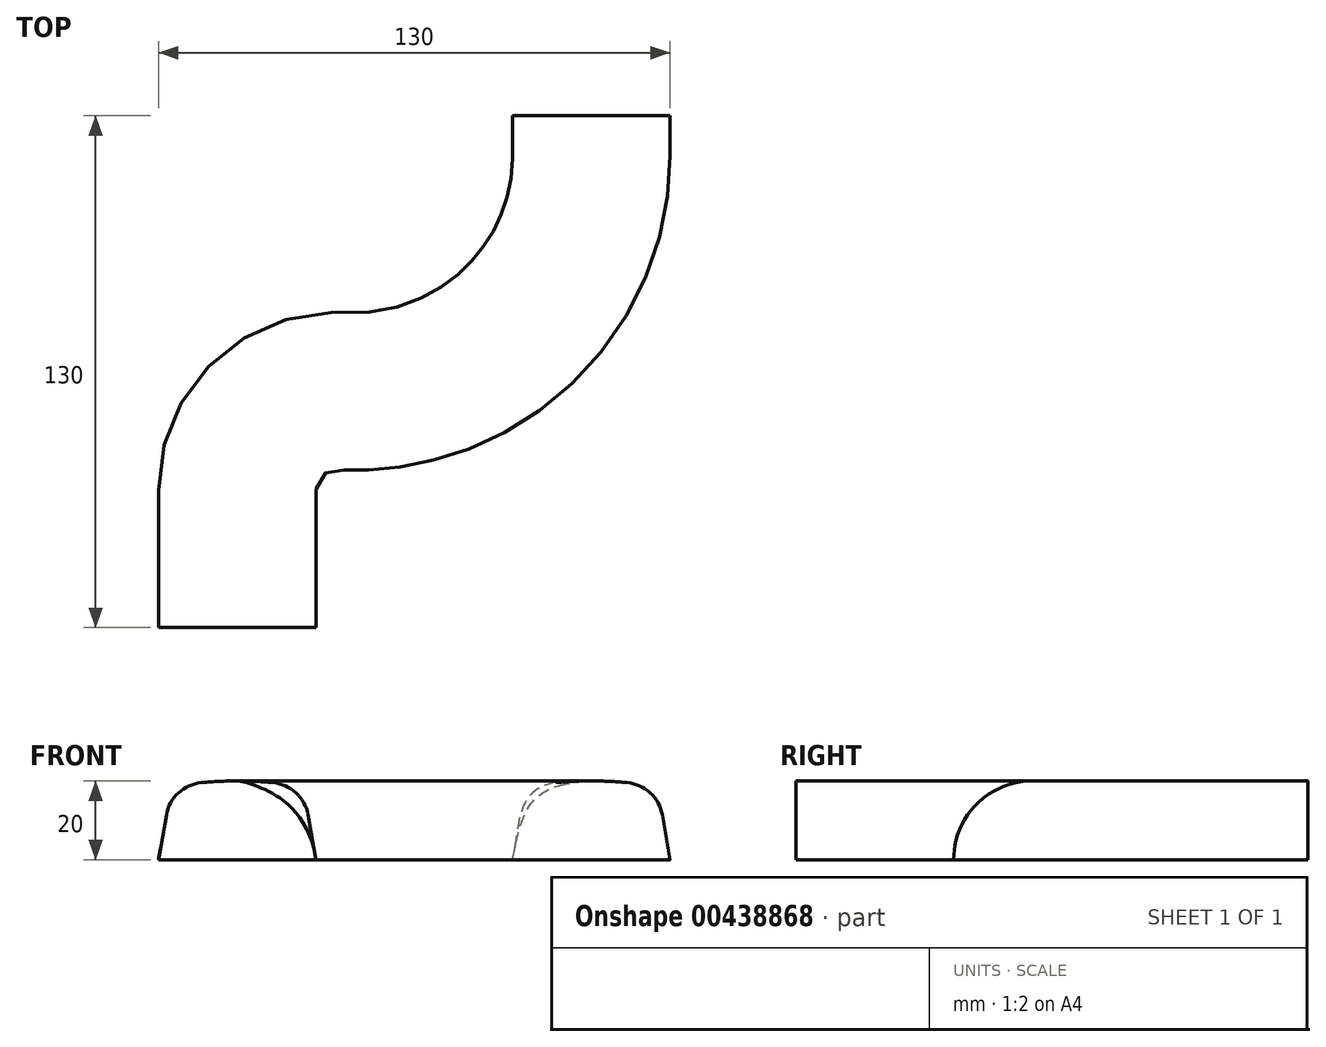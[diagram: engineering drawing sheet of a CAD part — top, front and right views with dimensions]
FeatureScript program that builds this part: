
annotation { "Feature Type Name" : "Feature", "Feature Type Description" : "" }
export const myFeature = defineFeature(function(context is Context, id is Id, definition is map)
    precondition{}
    {
        {
            var Q0;
            Q0=qCreatedBy(makeId("Top.planeOp"),FACE);
            var sketch = newSketch(context, id + "F0", { "sketchPlane" : qUnion([Q0])});
            skLineSegment(sketch, "E0", {"start": v(-30, -60) * mm, "end": v(-30, -25) * mm});
            skLineSegment(sketch, "E1", {"start": v(-5, 0) * mm, "end": v(0, 0) * mm});
            skLineSegment(sketch, "E2", {"start": v(60, 60) * mm, "end": v(60, 70) * mm});
            skArc(sketch, "E3.filletArc", {"start": v(0, 0) * mm, "mid": v(42.43, 17.57) * mm, "end": v(60, 60) * mm});
            skPoint(sketch, "E4.visualSharp", {"position": v(-30, 0) * mm});
            skArc(sketch, "E4.filletArc", {"start": v(-5, 0) * mm, "mid": v(-22.68, -7.32) * mm, "end": v(-30, -25) * mm});
            skSolve(sketch);
        }
        {
            var Q0;
            Q0=sQuery(id+"F0.wireOp",VERTEX,"E0.start");
            var Q1;
            Q1=sQuery(id+"F0.wireOp",EDGE,"E0");
            cPlane(context, id + "F1", {"entities" : qUnion([Q0, Q1]), "cplaneType" : CPlaneType.LINE_POINT, "offset" : 25 * mm, "width" : 150 * mm, "height" : 150 * mm});
        }
        {
            var Q0;
            Q0=sQuery(id+"F0.wireOp",VERTEX,"E2.end");
            var Q1;
            Q1=sQuery(id+"F0.wireOp",EDGE,"E2");
            cPlane(context, id + "F2", {"entities" : qUnion([Q0, Q1]), "cplaneType" : CPlaneType.LINE_POINT, "offset" : 25 * mm, "width" : 150 * mm, "height" : 150 * mm});
        }
        {
            var Q0;
            Q0=qCreatedBy(id+"F1.planeOp",FACE);
            var sketch = newSketch(context, id + "F3", { "sketchPlane" : qUnion([Q0])});
            skLineSegment(sketch, "E5", {"start": v(30, 0) * mm, "end": v(30, -10) * mm, "construction": true});
            skLineSegment(sketch, "E6.bottom", {"start": v(10, -20) * mm, "end": v(50, -20) * mm, "construction": true});
            skLineSegment(sketch, "E6.top", {"start": v(10, 0) * mm, "end": v(50, 0) * mm, "construction": true});
            skLineSegment(sketch, "E6.left", {"start": v(10, -20) * mm, "end": v(10, 0) * mm, "construction": true});
            skLineSegment(sketch, "E6.right", {"start": v(50, -20) * mm, "end": v(50, 0) * mm, "construction": true});
            skPoint(sketch, "E6.middle", {"position": v(30, -10) * mm});
            skLineSegment(sketch, "E7", {"start": v(50, -20) * mm, "end": v(48, -8.63) * mm});
            skLineSegment(sketch, "E8.MirrorCS", {"start": v(10, -20) * mm, "end": v(12, -8.63) * mm});
            skArc(sketch, "E9", {"start": v(39.05, -0.41) * mm, "mid": v(30, 0) * mm, "end": v(20.95, -0.41) * mm});
            skPoint(sketch, "E10.visualSharp", {"position": v(46.72, -1.4) * mm});
            skArc(sketch, "E10.filletArc", {"start": v(48, -8.63) * mm, "mid": v(44.92, -3) * mm, "end": v(39.05, -0.41) * mm});
            skPoint(sketch, "E11.visualSharp", {"position": v(13.28, -1.4) * mm});
            skArc(sketch, "E11.filletArc", {"start": v(20.95, -0.41) * mm, "mid": v(15.08, -3) * mm, "end": v(12, -8.63) * mm});
            skSolve(sketch);
        }
        {
            var Q0;
            Q0=qCreatedBy(makeId("Right.planeOp"),FACE);
            var sketch = newSketch(context, id + "F4", { "sketchPlane" : qUnion([Q0])});
            skLineSegment(sketch, "E12", {"start": v(0, 0) * mm, "end": v(0, -20) * mm, "construction": true});
            skArc(sketch, "E13", {"start": v(20, -20) * mm, "mid": v(0, 0) * mm, "end": v(-20, -20) * mm});
            skSolve(sketch);
        }
        {
            var Q0;
            Q0=qCreatedBy(id+"F2.planeOp",FACE);
            var sketch = newSketch(context, id + "F5", { "sketchPlane" : qUnion([Q0])});
            skLineSegment(sketch, "E14", {"start": v(-60, 0) * mm, "end": v(-60, -10) * mm, "construction": true});
            skLineSegment(sketch, "E15.bottom", {"start": v(-40, -20) * mm, "end": v(-80, -20) * mm, "construction": true});
            skLineSegment(sketch, "E15.top", {"start": v(-40, 0) * mm, "end": v(-80, 0) * mm, "construction": true});
            skLineSegment(sketch, "E15.left", {"start": v(-40, -20) * mm, "end": v(-40, 0) * mm, "construction": true});
            skLineSegment(sketch, "E15.right", {"start": v(-80, -20) * mm, "end": v(-80, 0) * mm, "construction": true});
            skPoint(sketch, "E15.middle", {"position": v(-60, -10) * mm});
            skLineSegment(sketch, "E16", {"start": v(-80, -20) * mm, "end": v(-78, -8.63) * mm});
            skLineSegment(sketch, "E17.MirrorCS", {"start": v(-40, -20) * mm, "end": v(-42, -8.63) * mm});
            skArc(sketch, "E18", {"start": v(-50.95, -0.41) * mm, "mid": v(-60, 0) * mm, "end": v(-69.05, -0.41) * mm});
            skPoint(sketch, "E19.visualSharp", {"position": v(-76.72, -1.4) * mm});
            skArc(sketch, "E19.filletArc", {"start": v(-69.05, -0.41) * mm, "mid": v(-74.92, -3) * mm, "end": v(-78, -8.63) * mm});
            skPoint(sketch, "E20.visualSharp", {"position": v(-43.28, -1.4) * mm});
            skArc(sketch, "E20.filletArc", {"start": v(-42, -8.63) * mm, "mid": v(-45.08, -3) * mm, "end": v(-50.95, -0.41) * mm});
            skSolve(sketch);
        }
        {
            var Q0;
            Q0=qCreatedBy(makeId("Top.planeOp"),FACE);
            cPlane(context, id + "F6", {"entities" : qUnion([Q0]), "cplaneType" : CPlaneType.OFFSET, "offset" : 20 * mm, "oppositeDirection" : true, "width" : 150 * mm, "height" : 150 * mm});
        }
        {
            var Q0;
            Q0=qCreatedBy(id+"F6.planeOp",FACE);
            var sketch = newSketch(context, id + "F7", { "sketchPlane" : qUnion([Q0])});
            skLineSegment(sketch, "E21.0", {"start": v(40, 60) * mm, "end": v(40, 70) * mm});
            skLineSegment(sketch, "E21.1", {"start": v(-50, -60) * mm, "end": v(-50, -25) * mm});
            skArc(sketch, "E21.2", {"start": v(-5, 20) * mm, "mid": v(-36.82, 6.82) * mm, "end": v(-50, -25) * mm});
            skLineSegment(sketch, "E21.3", {"start": v(-5, 20) * mm, "end": v(0, 20) * mm});
            skArc(sketch, "E21.4", {"start": v(0, 20) * mm, "mid": v(28.28, 31.72) * mm, "end": v(40, 60) * mm});
            skSolve(sketch);
        }
        {
            var Q0;
            Q0=qCreatedBy(id+"F6.planeOp",FACE);
            var sketch = newSketch(context, id + "F8", { "sketchPlane" : qUnion([Q0])});
            skLineSegment(sketch, "E22.0", {"start": v(80, 60) * mm, "end": v(80, 70) * mm});
            skLineSegment(sketch, "E22.1", {"start": v(-10, -60) * mm, "end": v(-10, -25) * mm});
            skArc(sketch, "E22.2", {"start": v(-5, -20) * mm, "mid": v(-8.54, -21.46) * mm, "end": v(-10, -25) * mm});
            skLineSegment(sketch, "E22.3", {"start": v(-5, -20) * mm, "end": v(0, -20) * mm});
            skArc(sketch, "E22.4", {"start": v(0, -20) * mm, "mid": v(56.57, 3.43) * mm, "end": v(80, 60) * mm});
            skSolve(sketch);
        }
        {
            var Q0;
            Q0 = qConstructionFilter(qBodyType(qCreatedBy(id + "F3" ,EDGE), BodyType.WIRE), ConstructionObject.NO);
            var Q1;
            Q1 = qConstructionFilter(qBodyType(qCreatedBy(id + "F4" ,EDGE), BodyType.WIRE), ConstructionObject.NO);
            var Q2;
            Q2 = qConstructionFilter(qBodyType(qCreatedBy(id + "F5" ,EDGE), BodyType.WIRE), ConstructionObject.NO);
            var Q3;
            Q3 = qConstructionFilter(qBodyType(qCreatedBy(id + "F0" ,EDGE), BodyType.WIRE), ConstructionObject.NO);
            var Q4;
            Q4 = qConstructionFilter(qBodyType(qCreatedBy(id + "F7" ,EDGE), BodyType.WIRE), ConstructionObject.NO);
            var Q5;
            Q5 = qConstructionFilter(qBodyType(qCreatedBy(id + "F8" ,EDGE), BodyType.WIRE), ConstructionObject.NO);
            loft(context, id + "F9", {"bodyType" : ToolBodyType.SURFACE, "addGuides" : true, "wireProfilesArray" : [{ "wireProfileEntities" : qUnion([Q0]) }, { "wireProfileEntities" : qUnion([Q1]) }, { "wireProfileEntities" : qUnion([Q2]) }], "guidesArray" : [{ "guideEntities" : qUnion([Q3]), "guideDerivativeType" : LoftGuideDerivativeType.DEFAULT, "guideDerivativeMagnitude" : 1 }, { "guideEntities" : qUnion([Q4]), "guideDerivativeType" : LoftGuideDerivativeType.DEFAULT, "guideDerivativeMagnitude" : 1 }, { "guideEntities" : qUnion([Q5]), "guideDerivativeType" : LoftGuideDerivativeType.DEFAULT, "guideDerivativeMagnitude" : 1 }]});
        }
    });
